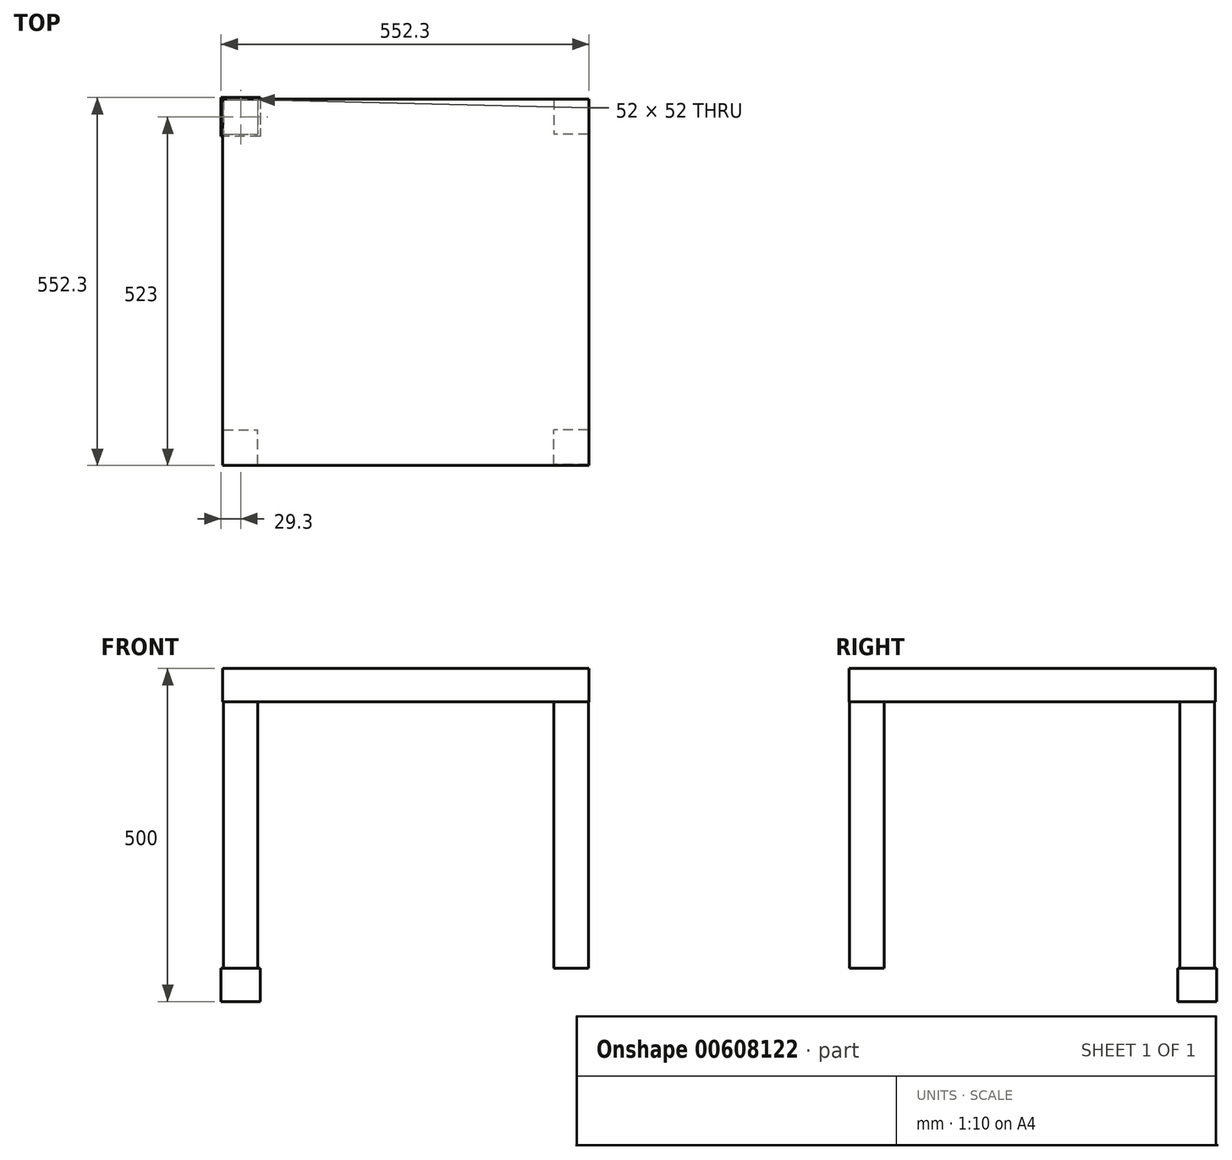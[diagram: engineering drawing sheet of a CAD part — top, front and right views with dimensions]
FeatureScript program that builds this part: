
annotation { "Feature Type Name" : "Feature", "Feature Type Description" : "" }
export const myFeature = defineFeature(function(context is Context, id is Id, definition is map)
    precondition{}
    {
        {
            var Q0;
            Q0=qCreatedBy(makeId("Top.planeOp"),FACE);
            var sketch = newSketch(context, id + "F0", { "sketchPlane" : qUnion([Q0])});
            skLineSegment(sketch, "E0.bottom", {"start": v(275, -275) * mm, "end": v(-275, -275) * mm});
            skLineSegment(sketch, "E0.top", {"start": v(275, 275) * mm, "end": v(-275, 275) * mm});
            skLineSegment(sketch, "E0.left", {"start": v(275, -275) * mm, "end": v(275, 275) * mm});
            skLineSegment(sketch, "E0.right", {"start": v(-275, -275) * mm, "end": v(-275, 275) * mm});
            skPoint(sketch, "E0.middle", {"position": v(0, 0) * mm});
            skSolve(sketch);
        }
        {
            var Q0;
            Q0=makeQuery(id+"F0.imprint","IMPRINT",FACE,{"disambiguationData":[TD([[makeQuery(id+"F0.imprint","IMPRINT",EDGE,{"derivedFrom":sQuery(id+"F0.wireOp",EDGE,"E0.bottom")}),-1.0]])]});
            extrude(context, id + "F1", {"entities" : qUnion([Q0]), "depth" : 50 * mm, "offsetDistance" : 25 * mm});
        }
        {
            var Q0;
            Q0=makeQuery(id+"F1.opExtrude","CAP_FACE",FACE,{"disambiguationData":[OSD([sQuery(id+"F0.wireOp",EDGE,"E0.bottom"),sQuery(id+"F0.wireOp",EDGE,"E0.top"),sQuery(id+"F0.wireOp",EDGE,"E0.left"),sQuery(id+"F0.wireOp",EDGE,"E0.right")])],"isStart":true});
            var sketch = newSketch(context, id + "F2", { "sketchPlane" : qUnion([Q0])});
            skLineSegment(sketch, "E1.bottom", {"start": v(-275, 275) * mm, "end": v(-274, 275) * mm});
            skLineSegment(sketch, "E1.top", {"start": v(-275, 274) * mm, "end": v(-274, 274) * mm});
            skLineSegment(sketch, "E1.left", {"start": v(-275, 275) * mm, "end": v(-275, 274) * mm});
            skLineSegment(sketch, "E1.right", {"start": v(-274, 275) * mm, "end": v(-274, 274) * mm});
            skLineSegment(sketch, "E2.bottom", {"start": v(275, 275) * mm, "end": v(274, 275) * mm});
            skLineSegment(sketch, "E2.top", {"start": v(275, 274) * mm, "end": v(274, 274) * mm});
            skLineSegment(sketch, "E2.left", {"start": v(275, 275) * mm, "end": v(275, 274) * mm});
            skLineSegment(sketch, "E2.right", {"start": v(274, 275) * mm, "end": v(274, 274) * mm});
            skLineSegment(sketch, "E3.bottom", {"start": v(275, -275) * mm, "end": v(274, -275) * mm});
            skLineSegment(sketch, "E3.top", {"start": v(275, -274) * mm, "end": v(274, -274) * mm});
            skLineSegment(sketch, "E3.left", {"start": v(275, -275) * mm, "end": v(275, -274) * mm});
            skLineSegment(sketch, "E3.right", {"start": v(274, -275) * mm, "end": v(274, -274) * mm});
            skLineSegment(sketch, "E4.bottom", {"start": v(-275, -275) * mm, "end": v(-274, -275) * mm});
            skLineSegment(sketch, "E4.top", {"start": v(-275, -274) * mm, "end": v(-274, -274) * mm});
            skLineSegment(sketch, "E4.left", {"start": v(-275, -275) * mm, "end": v(-275, -274) * mm});
            skLineSegment(sketch, "E4.right", {"start": v(-274, -275) * mm, "end": v(-274, -274) * mm});
            skLineSegment(sketch, "E5.bottom", {"start": v(-274, 274) * mm, "end": v(-222, 274) * mm});
            skLineSegment(sketch, "E5.top", {"start": v(-274, 222) * mm, "end": v(-222, 222) * mm});
            skLineSegment(sketch, "E5.left", {"start": v(-274, 274) * mm, "end": v(-274, 222) * mm});
            skLineSegment(sketch, "E5.right", {"start": v(-222, 274) * mm, "end": v(-222, 222) * mm});
            skLineSegment(sketch, "E6.bottom", {"start": v(274, 274) * mm, "end": v(222, 274) * mm});
            skLineSegment(sketch, "E6.top", {"start": v(274, 222) * mm, "end": v(222, 222) * mm});
            skLineSegment(sketch, "E6.left", {"start": v(274, 274) * mm, "end": v(274, 222) * mm});
            skLineSegment(sketch, "E6.right", {"start": v(222, 274) * mm, "end": v(222, 222) * mm});
            skLineSegment(sketch, "E7.bottom", {"start": v(274, -274) * mm, "end": v(222, -274) * mm});
            skLineSegment(sketch, "E7.top", {"start": v(274, -222) * mm, "end": v(222, -222) * mm});
            skLineSegment(sketch, "E7.left", {"start": v(274, -274) * mm, "end": v(274, -222) * mm});
            skLineSegment(sketch, "E7.right", {"start": v(222, -274) * mm, "end": v(222, -222) * mm});
            skLineSegment(sketch, "E8.bottom", {"start": v(-274, -274) * mm, "end": v(-222, -274) * mm});
            skLineSegment(sketch, "E8.top", {"start": v(-274, -222) * mm, "end": v(-222, -222) * mm});
            skLineSegment(sketch, "E8.left", {"start": v(-274, -274) * mm, "end": v(-274, -222) * mm});
            skLineSegment(sketch, "E8.right", {"start": v(-222, -274) * mm, "end": v(-222, -222) * mm});
            skSolve(sketch);
        }
        {
            var Q0;
            Q0=makeQuery(id+"F2.imprint","IMPRINT",FACE,{"disambiguationData":[TD([[makeQuery(id+"F2.imprint","IMPRINT",EDGE,{"derivedFrom":sQuery(id+"F2.wireOp",EDGE,"E5.bottom")}),-1.0]])]});
            var Q1;
            Q1=makeQuery(id+"F2.imprint","IMPRINT",FACE,{"disambiguationData":[TD([[makeQuery(id+"F2.imprint","IMPRINT",EDGE,{"derivedFrom":sQuery(id+"F2.wireOp",EDGE,"E6.bottom")}),1.0]])]});
            var Q2;
            Q2=makeQuery(id+"F2.imprint","IMPRINT",FACE,{"disambiguationData":[TD([[makeQuery(id+"F2.imprint","IMPRINT",EDGE,{"derivedFrom":sQuery(id+"F2.wireOp",EDGE,"E7.bottom")}),-1.0]])]});
            var Q3;
            Q3=makeQuery(id+"F2.imprint","IMPRINT",FACE,{"disambiguationData":[TD([[makeQuery(id+"F2.imprint","IMPRINT",EDGE,{"derivedFrom":sQuery(id+"F2.wireOp",EDGE,"E8.bottom")}),1.0]])]});
            extrude(context, id + "F3", {"entities" : qUnion([Q0, Q1, Q2, Q3]), "operationType" : NewBodyOperationType.ADD, "depth" : 400 * mm, "offsetDistance" : 25 * mm});
        }
        {
            var Q0;
            Q0=makeQuery(id+"F3.opExtrude","CAP_FACE",FACE,{"disambiguationData":[OSD([sQuery(id+"F2.wireOp",EDGE,"E8.bottom"),sQuery(id+"F2.wireOp",EDGE,"E8.top"),sQuery(id+"F2.wireOp",EDGE,"E8.left"),sQuery(id+"F2.wireOp",EDGE,"E8.right")])],"isStart":false});
            var sketch = newSketch(context, id + "F4", { "sketchPlane" : qUnion([Q0])});
            skLineSegment(sketch, "E9.0", {"start": v(-218.7, -218.7) * mm, "end": v(-277.3, -218.7) * mm});
            skLineSegment(sketch, "E9.1", {"start": v(-218.7, -277.3) * mm, "end": v(-218.7, -218.7) * mm});
            skLineSegment(sketch, "E9.2", {"start": v(-277.3, -277.3) * mm, "end": v(-218.7, -277.3) * mm});
            skLineSegment(sketch, "E9.3", {"start": v(-277.3, -218.7) * mm, "end": v(-277.3, -277.3) * mm});
            skSolve(sketch);
        }
        {
            var Q0;
            Q0 = qSketchRegion(id + "F4", true);
            extrude(context, id + "F5", {"entities" : qUnion([Q0]), "operationType" : NewBodyOperationType.ADD, "depth" : 50 * mm, "offsetDistance" : 25 * mm});
        }
    });
